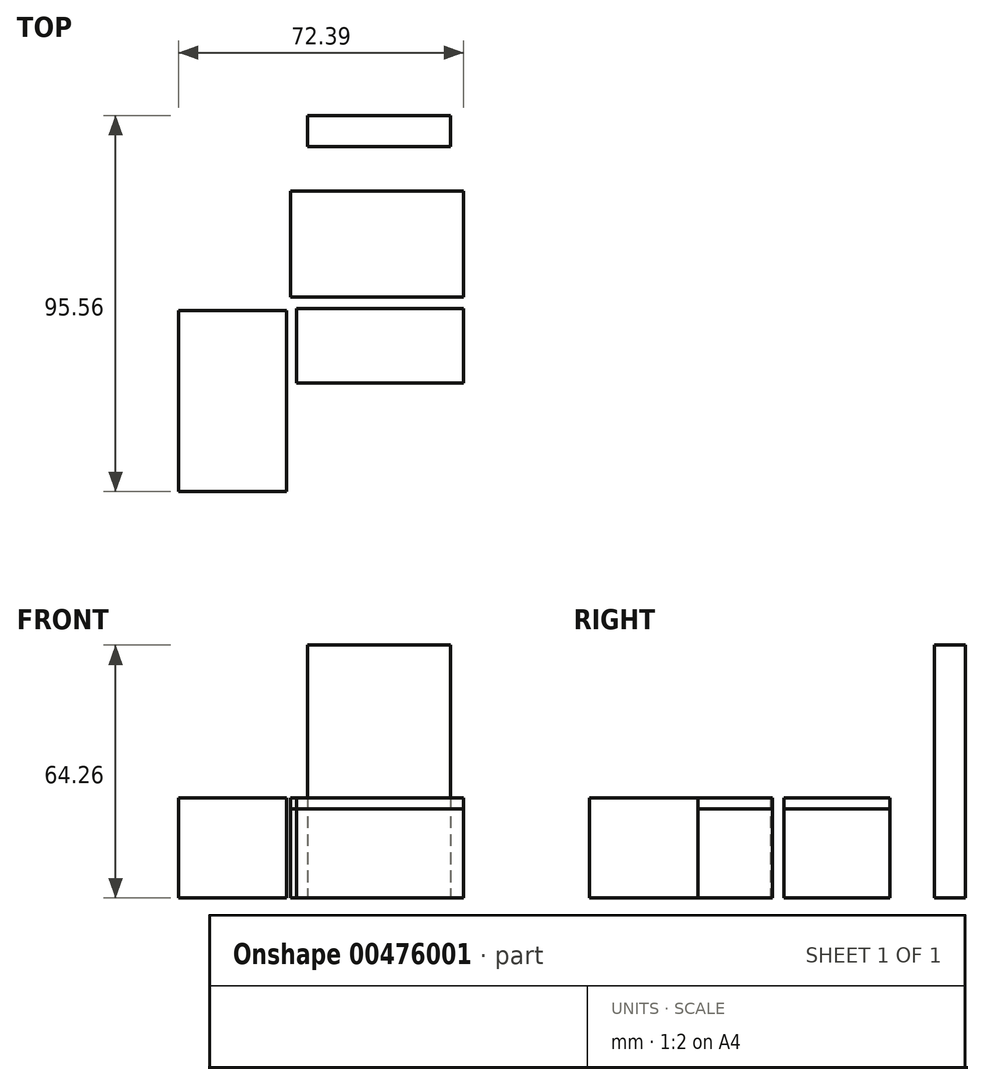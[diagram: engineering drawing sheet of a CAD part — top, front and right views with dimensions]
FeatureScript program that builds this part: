
annotation { "Feature Type Name" : "Feature", "Feature Type Description" : "" }
export const myFeature = defineFeature(function(context is Context, id is Id, definition is map)
    precondition{}
    {
        {
            var Q0;
            Q0=qCreatedBy(makeId("Top.planeOp"),FACE);
            var sketch = newSketch(context, id + "F0", { "sketchPlane" : qUnion([Q0])});
            skLineSegment(sketch, "E0.bottom", {"start": v(-23.16, 26.97) * mm, "end": v(20.73, 26.97) * mm});
            skLineSegment(sketch, "E0.top", {"start": v(-23.16, 0) * mm, "end": v(20.73, 0) * mm});
            skLineSegment(sketch, "E0.left", {"start": v(-23.16, 26.97) * mm, "end": v(-23.16, 0) * mm});
            skLineSegment(sketch, "E0.right", {"start": v(20.73, 26.97) * mm, "end": v(20.73, 0) * mm});
            skLineSegment(sketch, "E1.bottom", {"start": v(-21.64, -21.8) * mm, "end": v(20.73, -21.8) * mm});
            skLineSegment(sketch, "E1.top", {"start": v(-21.64, -2.9) * mm, "end": v(20.73, -2.9) * mm});
            skLineSegment(sketch, "E1.left", {"start": v(-21.64, -21.8) * mm, "end": v(-21.64, -2.9) * mm});
            skLineSegment(sketch, "E1.right", {"start": v(20.73, -21.8) * mm, "end": v(20.73, -2.9) * mm});
            skSolve(sketch);
        }
        {
            var Q0;
            Q0 = qSketchRegion(id + "F0", true);
            extrude(context, id + "F1", {"entities" : qUnion([Q0]), "depth" : 25.4 * mm});
        }
        {
            var Q0;
            Q0 = qSketchRegion(id + "F0", true);
            extrude(context, id + "F2", {"entities" : qUnion([Q0]), "depth" : 22.6 * mm});
        }
        {
            var Q0;
            Q0=qCreatedBy(makeId("Top.planeOp"),FACE);
            var sketch = newSketch(context, id + "F3", { "sketchPlane" : qUnion([Q0])});
            skLineSegment(sketch, "E2.bottom", {"start": v(-18.9, 46.18) * mm, "end": v(17.37, 46.18) * mm});
            skLineSegment(sketch, "E2.top", {"start": v(-18.9, 38.25) * mm, "end": v(17.37, 38.25) * mm});
            skLineSegment(sketch, "E2.left", {"start": v(-18.9, 46.18) * mm, "end": v(-18.9, 38.25) * mm});
            skLineSegment(sketch, "E2.right", {"start": v(17.37, 46.18) * mm, "end": v(17.37, 38.25) * mm});
            skSolve(sketch);
        }
        {
            var Q0;
            Q0 = qSketchRegion(id + "F3", true);
            extrude(context, id + "F4", {"entities" : qUnion([Q0]), "depth" : 64.26 * mm});
        }
        {
            var Q0;
            Q0=qCreatedBy(makeId("Top.planeOp"),FACE);
            var sketch = newSketch(context, id + "F5", { "sketchPlane" : qUnion([Q0])});
            skLineSegment(sketch, "E3.bottom", {"start": v(-51.66, -49.38) * mm, "end": v(-24.23, -49.38) * mm});
            skLineSegment(sketch, "E3.top", {"start": v(-51.66, -3.35) * mm, "end": v(-24.23, -3.35) * mm});
            skLineSegment(sketch, "E3.left", {"start": v(-51.66, -49.38) * mm, "end": v(-51.66, -3.35) * mm});
            skLineSegment(sketch, "E3.right", {"start": v(-24.23, -49.38) * mm, "end": v(-24.23, -3.35) * mm});
            skSolve(sketch);
        }
        {
            var Q0;
            Q0 = qSketchRegion(id + "F5", true);
            extrude(context, id + "F6", {"entities" : qUnion([Q0]), "depth" : 25.4 * mm});
        }
    });
